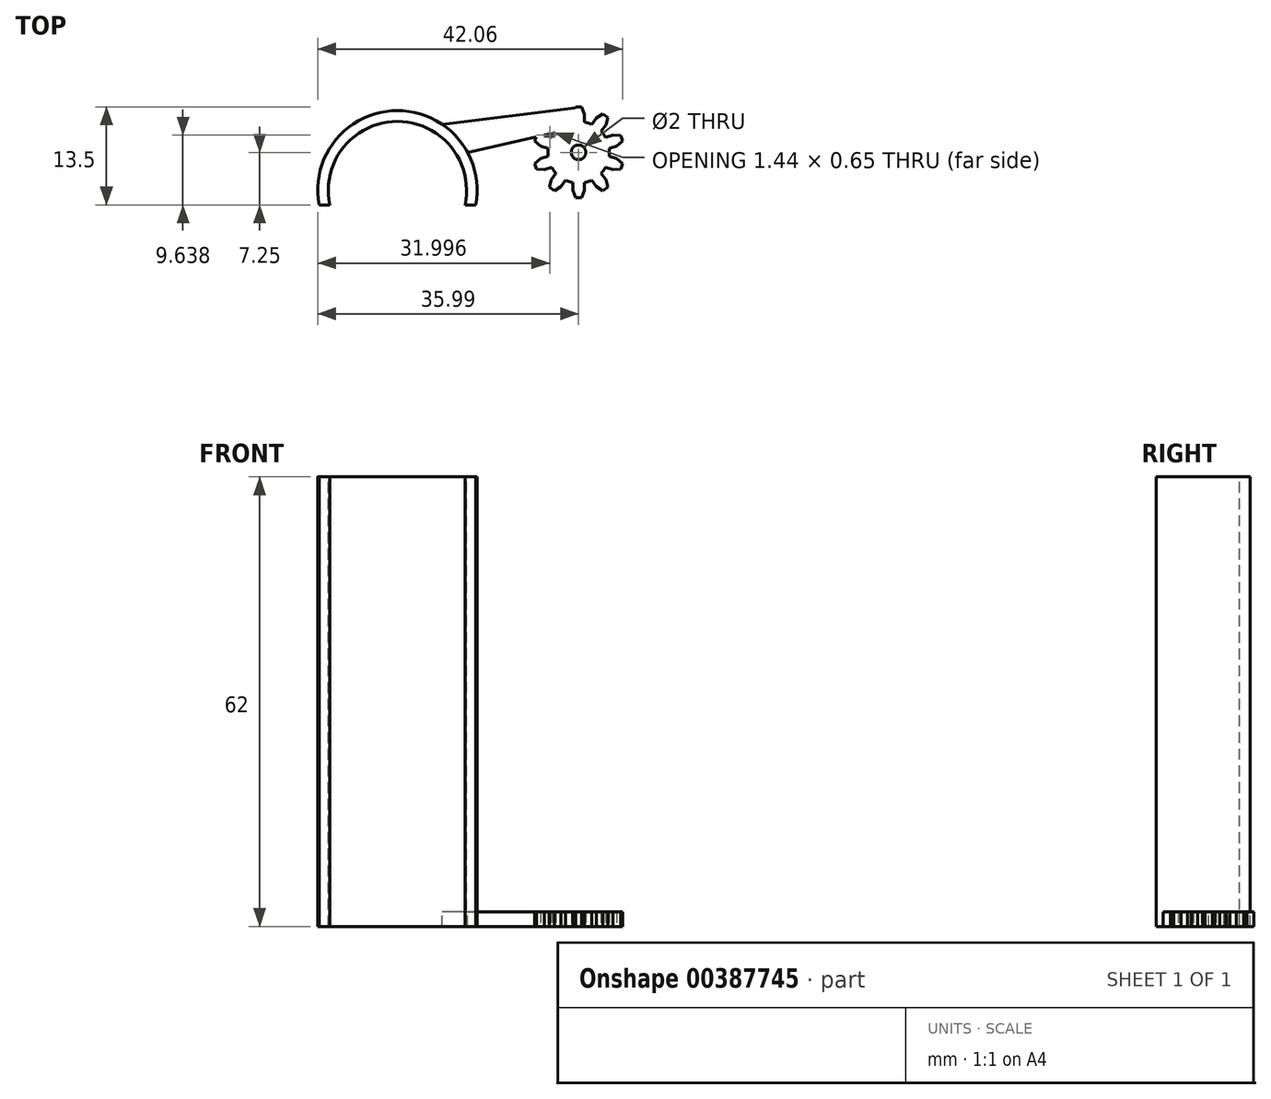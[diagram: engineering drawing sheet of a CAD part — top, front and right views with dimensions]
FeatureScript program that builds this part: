
annotation { "Feature Type Name" : "Feature", "Feature Type Description" : "" }
export const myFeature = defineFeature(function(context is Context, id is Id, definition is map)
    precondition{}
    {
        {
            var Q0;
            Q0=qCreatedBy(makeId("Top.planeOp"),FACE);
            var sketch = newSketch(context, id + "F0", { "sketchPlane" : qUnion([Q0])});
            skArc(sketch, "E0", {"start": v(-3.1, 2.9) * mm, "mid": v(-3.44, 2.5) * mm, "end": v(-3.72, 2.06) * mm});
            skLineSegment(sketch, "E1", {"start": v(-1.31, 4.04) * mm, "end": v(0, 0) * mm, "construction": true});
            skLineSegment(sketch, "E2", {"start": v(1.31, 4.04) * mm, "end": v(0, 0) * mm, "construction": true});
            skLineSegment(sketch, "E3", {"start": v(0, 0) * mm, "end": v(0, 4.25) * mm, "construction": true});
            skLineSegment(sketch, "E4", {"start": v(0, 4.25) * mm, "end": v(1.31, 4.04) * mm, "construction": true});
            skLineSegment(sketch, "E5", {"start": v(0, 4.25) * mm, "end": v(-1.31, 4.04) * mm, "construction": true});
            skLineSegment(sketch, "E6", {"start": v(-0.81, 5.26) * mm, "end": v(-0.4, 6.25) * mm});
            skLineSegment(sketch, "E7", {"start": v(0.4, 6.25) * mm, "end": v(0.81, 5.26) * mm});
            skLineSegment(sketch, "E8", {"start": v(0, 4.25) * mm, "end": v(0, 7.25) * mm, "construction": true});
            skLineSegment(sketch, "E9", {"start": v(-0.4, 6.25) * mm, "end": v(0.4, 6.25) * mm});
            skLineSegment(sketch, "E10", {"start": v(-1.31, 4.04) * mm, "end": v(1.31, 4.04) * mm, "construction": true});
            skLineSegment(sketch, "E11", {"start": v(0.81, 5.26) * mm, "end": v(0.81, 4.17) * mm});
            skLineSegment(sketch, "E12", {"start": v(-0.81, 5.26) * mm, "end": v(-0.81, 4.17) * mm});
            skLineSegment(sketch, "E13.1.0", {"start": v(-4, 4.82) * mm, "end": v(-3.34, 5.3) * mm});
            skLineSegment(sketch, "E13.1.1", {"start": v(-3.75, 3.78) * mm, "end": v(-4, 4.82) * mm});
            skLineSegment(sketch, "E13.1.2", {"start": v(-3.75, 3.78) * mm, "end": v(-3.1, 2.9) * mm});
            skLineSegment(sketch, "E13.1.3", {"start": v(-3.34, 5.3) * mm, "end": v(-2.44, 4.74) * mm});
            skLineSegment(sketch, "E13.1.4", {"start": v(-2.44, 4.74) * mm, "end": v(-1.8, 3.85) * mm});
            skLineSegment(sketch, "E13.2.0", {"start": v(-6.07, 1.54) * mm, "end": v(-5.82, 2.32) * mm});
            skLineSegment(sketch, "E13.2.1", {"start": v(-5.26, 0.85) * mm, "end": v(-6.07, 1.54) * mm});
            skLineSegment(sketch, "E13.2.2", {"start": v(-5.26, 0.85) * mm, "end": v(-4.22, 0.52) * mm});
            skLineSegment(sketch, "E13.2.3", {"start": v(-5.82, 2.32) * mm, "end": v(-4.75, 2.4) * mm});
            skLineSegment(sketch, "E13.2.4", {"start": v(-4.75, 2.4) * mm, "end": v(-3.72, 2.06) * mm});
            skLineSegment(sketch, "E13.3.0", {"start": v(-5.82, -2.32) * mm, "end": v(-6.07, -1.54) * mm});
            skLineSegment(sketch, "E13.3.1", {"start": v(-4.75, -2.4) * mm, "end": v(-5.82, -2.32) * mm});
            skLineSegment(sketch, "E13.3.2", {"start": v(-4.75, -2.4) * mm, "end": v(-3.72, -2.06) * mm});
            skLineSegment(sketch, "E13.3.3", {"start": v(-6.07, -1.54) * mm, "end": v(-5.26, -0.85) * mm});
            skLineSegment(sketch, "E13.3.4", {"start": v(-5.26, -0.85) * mm, "end": v(-4.22, -0.52) * mm});
            skLineSegment(sketch, "E13.4.0", {"start": v(-3.34, -5.3) * mm, "end": v(-4, -4.82) * mm});
            skLineSegment(sketch, "E13.4.1", {"start": v(-2.44, -4.74) * mm, "end": v(-3.34, -5.3) * mm});
            skLineSegment(sketch, "E13.4.2", {"start": v(-2.44, -4.74) * mm, "end": v(-1.8, -3.85) * mm});
            skLineSegment(sketch, "E13.4.3", {"start": v(-4, -4.82) * mm, "end": v(-3.75, -3.78) * mm});
            skLineSegment(sketch, "E13.4.4", {"start": v(-3.75, -3.78) * mm, "end": v(-3.1, -2.9) * mm});
            skLineSegment(sketch, "E13.5.0", {"start": v(0.4, -6.25) * mm, "end": v(-0.4, -6.25) * mm});
            skLineSegment(sketch, "E13.5.1", {"start": v(0.81, -5.26) * mm, "end": v(0.4, -6.25) * mm});
            skLineSegment(sketch, "E13.5.2", {"start": v(0.81, -5.26) * mm, "end": v(0.81, -4.17) * mm});
            skLineSegment(sketch, "E13.5.3", {"start": v(-0.4, -6.25) * mm, "end": v(-0.81, -5.26) * mm});
            skLineSegment(sketch, "E13.5.4", {"start": v(-0.81, -5.26) * mm, "end": v(-0.81, -4.17) * mm});
            skLineSegment(sketch, "E13.6.0", {"start": v(4, -4.82) * mm, "end": v(3.34, -5.3) * mm});
            skLineSegment(sketch, "E13.6.1", {"start": v(3.75, -3.78) * mm, "end": v(4, -4.82) * mm});
            skLineSegment(sketch, "E13.6.2", {"start": v(3.75, -3.78) * mm, "end": v(3.1, -2.9) * mm});
            skLineSegment(sketch, "E13.6.3", {"start": v(3.34, -5.3) * mm, "end": v(2.44, -4.74) * mm});
            skLineSegment(sketch, "E13.6.4", {"start": v(2.44, -4.74) * mm, "end": v(1.8, -3.85) * mm});
            skLineSegment(sketch, "E13.7.0", {"start": v(6.07, -1.54) * mm, "end": v(5.82, -2.32) * mm});
            skLineSegment(sketch, "E13.7.1", {"start": v(5.26, -0.85) * mm, "end": v(6.07, -1.54) * mm});
            skLineSegment(sketch, "E13.7.2", {"start": v(5.26, -0.85) * mm, "end": v(4.22, -0.52) * mm});
            skLineSegment(sketch, "E13.7.3", {"start": v(5.82, -2.32) * mm, "end": v(4.75, -2.4) * mm});
            skLineSegment(sketch, "E13.7.4", {"start": v(4.75, -2.4) * mm, "end": v(3.72, -2.06) * mm});
            skLineSegment(sketch, "E13.8.0", {"start": v(5.82, 2.32) * mm, "end": v(6.07, 1.54) * mm});
            skLineSegment(sketch, "E13.8.1", {"start": v(4.75, 2.4) * mm, "end": v(5.82, 2.32) * mm});
            skLineSegment(sketch, "E13.8.2", {"start": v(4.75, 2.4) * mm, "end": v(3.72, 2.06) * mm});
            skLineSegment(sketch, "E13.8.3", {"start": v(6.07, 1.54) * mm, "end": v(5.26, 0.85) * mm});
            skLineSegment(sketch, "E13.8.4", {"start": v(5.26, 0.85) * mm, "end": v(4.22, 0.52) * mm});
            skLineSegment(sketch, "E13.9.0", {"start": v(3.34, 5.3) * mm, "end": v(4, 4.82) * mm});
            skLineSegment(sketch, "E13.9.1", {"start": v(2.44, 4.74) * mm, "end": v(3.34, 5.3) * mm});
            skLineSegment(sketch, "E13.9.2", {"start": v(2.44, 4.74) * mm, "end": v(1.8, 3.85) * mm});
            skLineSegment(sketch, "E13.9.3", {"start": v(4, 4.82) * mm, "end": v(3.75, 3.78) * mm});
            skLineSegment(sketch, "E13.9.4", {"start": v(3.75, 3.78) * mm, "end": v(3.1, 2.9) * mm});
            skCircle(sketch, "E14", {"center": v(0, 0) * mm, "radius": 1 * mm});
            skArc(sketch, "E15.trimOffspring", {"start": v(-4.22, 0.52) * mm, "mid": v(-4.25, 0) * mm, "end": v(-4.22, -0.52) * mm});
            skArc(sketch, "E16.trimOffspring", {"start": v(-3.72, -2.06) * mm, "mid": v(-3.44, -2.5) * mm, "end": v(-3.1, -2.9) * mm});
            skArc(sketch, "E17.trimOffspring", {"start": v(-1.8, -3.85) * mm, "mid": v(-1.31, -4.04) * mm, "end": v(-0.81, -4.17) * mm});
            skArc(sketch, "E18.trimOffspring", {"start": v(0.81, -4.17) * mm, "mid": v(1.31, -4.04) * mm, "end": v(1.8, -3.85) * mm});
            skArc(sketch, "E19.trimOffspring", {"start": v(3.1, -2.9) * mm, "mid": v(3.44, -2.5) * mm, "end": v(3.72, -2.06) * mm});
            skArc(sketch, "E20.trimOffspring", {"start": v(4.22, -0.52) * mm, "mid": v(4.25, 0) * mm, "end": v(4.22, 0.52) * mm});
            skArc(sketch, "E21.trimOffspring", {"start": v(3.72, 2.06) * mm, "mid": v(3.44, 2.5) * mm, "end": v(3.1, 2.9) * mm});
            skArc(sketch, "E22.trimOffspring", {"start": v(1.8, 3.85) * mm, "mid": v(1.31, 4.04) * mm, "end": v(0.81, 4.17) * mm});
            skArc(sketch, "E23.trimOffspring", {"start": v(-0.81, 4.17) * mm, "mid": v(-1.31, 4.04) * mm, "end": v(-1.8, 3.85) * mm});
            skSolve(sketch);
        }
        {
            var Q0;
            Q0=makeQuery(id+"F0.imprint","IMPRINT",FACE,{"disambiguationData":[TD([[makeQuery(id+"F0.imprint","IMPRINT",EDGE,{"derivedFrom":sQuery(id+"F0.wireOp",EDGE,"E0")}),1.0]])]});
            extrude(context, id + "F1", {"entities" : qUnion([Q0]), "depth" : 2 * mm});
        }
        {
            var Q0;
            Q0=makeQuery(id+"F1.opExtrude","CAP_FACE",FACE,{"disambiguationData":[OSD([sQuery(id+"F0.wireOp",EDGE,"E0"),sQuery(id+"F0.wireOp",EDGE,"E6"),sQuery(id+"F0.wireOp",EDGE,"E7"),sQuery(id+"F0.wireOp",EDGE,"E9"),sQuery(id+"F0.wireOp",EDGE,"E11"),sQuery(id+"F0.wireOp",EDGE,"E12"),sQuery(id+"F0.wireOp",EDGE,"E13.1.0"),sQuery(id+"F0.wireOp",EDGE,"E13.1.1"),sQuery(id+"F0.wireOp",EDGE,"E13.1.2"),sQuery(id+"F0.wireOp",EDGE,"E13.1.3"),sQuery(id+"F0.wireOp",EDGE,"E13.1.4"),sQuery(id+"F0.wireOp",EDGE,"E13.2.0"),sQuery(id+"F0.wireOp",EDGE,"E13.2.1"),sQuery(id+"F0.wireOp",EDGE,"E13.2.2"),sQuery(id+"F0.wireOp",EDGE,"E13.2.3"),sQuery(id+"F0.wireOp",EDGE,"E13.2.4"),sQuery(id+"F0.wireOp",EDGE,"E13.3.0"),sQuery(id+"F0.wireOp",EDGE,"E13.3.1"),sQuery(id+"F0.wireOp",EDGE,"E13.3.2"),sQuery(id+"F0.wireOp",EDGE,"E13.3.3"),sQuery(id+"F0.wireOp",EDGE,"E13.3.4"),sQuery(id+"F0.wireOp",EDGE,"E13.4.0"),sQuery(id+"F0.wireOp",EDGE,"E13.4.1"),sQuery(id+"F0.wireOp",EDGE,"E13.4.2"),sQuery(id+"F0.wireOp",EDGE,"E13.4.3"),sQuery(id+"F0.wireOp",EDGE,"E13.4.4"),sQuery(id+"F0.wireOp",EDGE,"E13.5.0"),sQuery(id+"F0.wireOp",EDGE,"E13.5.1"),sQuery(id+"F0.wireOp",EDGE,"E13.5.2"),sQuery(id+"F0.wireOp",EDGE,"E13.5.3"),sQuery(id+"F0.wireOp",EDGE,"E13.5.4"),sQuery(id+"F0.wireOp",EDGE,"E13.6.0"),sQuery(id+"F0.wireOp",EDGE,"E13.6.1"),sQuery(id+"F0.wireOp",EDGE,"E13.6.2"),sQuery(id+"F0.wireOp",EDGE,"E13.6.3"),sQuery(id+"F0.wireOp",EDGE,"E13.6.4"),sQuery(id+"F0.wireOp",EDGE,"E13.7.0"),sQuery(id+"F0.wireOp",EDGE,"E13.7.1"),sQuery(id+"F0.wireOp",EDGE,"E13.7.2"),sQuery(id+"F0.wireOp",EDGE,"E13.7.3"),sQuery(id+"F0.wireOp",EDGE,"E13.7.4"),sQuery(id+"F0.wireOp",EDGE,"E13.8.0"),sQuery(id+"F0.wireOp",EDGE,"E13.8.1"),sQuery(id+"F0.wireOp",EDGE,"E13.8.2"),sQuery(id+"F0.wireOp",EDGE,"E13.8.3"),sQuery(id+"F0.wireOp",EDGE,"E13.8.4"),sQuery(id+"F0.wireOp",EDGE,"E13.9.0"),sQuery(id+"F0.wireOp",EDGE,"E13.9.1"),sQuery(id+"F0.wireOp",EDGE,"E13.9.2"),sQuery(id+"F0.wireOp",EDGE,"E13.9.3"),sQuery(id+"F0.wireOp",EDGE,"E13.9.4"),sQuery(id+"F0.wireOp",EDGE,"E14"),sQuery(id+"F0.wireOp",EDGE,"E15.trimOffspring"),sQuery(id+"F0.wireOp",EDGE,"E16.trimOffspring"),sQuery(id+"F0.wireOp",EDGE,"E17.trimOffspring"),sQuery(id+"F0.wireOp",EDGE,"E18.trimOffspring"),sQuery(id+"F0.wireOp",EDGE,"E19.trimOffspring"),sQuery(id+"F0.wireOp",EDGE,"E20.trimOffspring"),sQuery(id+"F0.wireOp",EDGE,"E21.trimOffspring"),sQuery(id+"F0.wireOp",EDGE,"E22.trimOffspring"),sQuery(id+"F0.wireOp",EDGE,"E23.trimOffspring")])],"isStart":false});
            var sketch = newSketch(context, id + "F2", { "sketchPlane" : qUnion([Q0])});
            skArc(sketch, "E24", {"start": v(-15.68, -7.25) * mm, "mid": v(-24.99, 4.27) * mm, "end": v(-34.3, -7.25) * mm});
            skArc(sketch, "E25", {"start": v(-14.17, -7.25) * mm, "mid": v(-14.12, -3.53) * mm, "end": v(-15.32, 0) * mm});
            skLineSegment(sketch, "E26", {"start": v(-35.8, -7.25) * mm, "end": v(-34.3, -7.25) * mm});
            skLineSegment(sketch, "E27", {"start": v(-15.68, -7.25) * mm, "end": v(-14.17, -7.25) * mm});
            skLineSegment(sketch, "E28", {"start": v(-15.32, 0) * mm, "end": v(1.8, 3.85) * mm});
            skLineSegment(sketch, "E29", {"start": v(1.8, 3.85) * mm, "end": v(0.4, 6.25) * mm});
            skLineSegment(sketch, "E30", {"start": v(0.4, 6.25) * mm, "end": v(-18.81, 3.85) * mm});
            skArc(sketch, "E31.trimOffspring", {"start": v(-18.81, 3.85) * mm, "mid": v(-31, 3.96) * mm, "end": v(-35.8, -7.25) * mm});
            skSolve(sketch);
        }
        {
            var Q0;
            Q0=makeQuery(id+"F2.imprint","IMPRINT",FACE,{"disambiguationData":[TD([[makeQuery(id+"F2.imprint","IMPRINT",EDGE,{"derivedFrom":sQuery(id+"F2.wireOp",EDGE,"E24")}),-1.0]])]});
            extrude(context, id + "F3", {"entities" : qUnion([Q0]), "operationType" : NewBodyOperationType.ADD, "oppositeDirection" : true, "depth" : 2 * mm});
        }
        {
            var Q0;
            {var subQ0=sQuery(id+"F0.wireOp",EDGE,"E23.trimOffspring");var subQ1=sQuery(id+"F0.wireOp",EDGE,"E13.2.4");var subQ2=sQuery(id+"F0.wireOp",EDGE,"E13.2.3");var subQ3=sQuery(id+"F0.wireOp",EDGE,"E13.2.0");var subQ4=sQuery(id+"F0.wireOp",EDGE,"E13.1.4");var subQ5=sQuery(id+"F0.wireOp",EDGE,"E13.1.3");var subQ6=sQuery(id+"F0.wireOp",EDGE,"E13.1.2");var subQ7=sQuery(id+"F0.wireOp",EDGE,"E13.1.1");var subQ8=sQuery(id+"F0.wireOp",EDGE,"E13.1.0");var subQ9=sQuery(id+"F0.wireOp",EDGE,"E12");var subQ10=sQuery(id+"F0.wireOp",EDGE,"E6");var subQ11=sQuery(id+"F0.wireOp",EDGE,"E0");Q0=makeQuery(id+"F3.boolean.opBoolean","MERGE",FACE,{"derivedFrom":[makeQuery(id+"F1.opExtrude","CAP_FACE",FACE,{"disambiguationData":[OSD([subQ11,subQ10,sQuery(id+"F0.wireOp",EDGE,"E7"),sQuery(id+"F0.wireOp",EDGE,"E9"),sQuery(id+"F0.wireOp",EDGE,"E11"),subQ9,subQ8,subQ7,subQ6,subQ5,subQ4,subQ3,sQuery(id+"F0.wireOp",EDGE,"E13.2.1"),sQuery(id+"F0.wireOp",EDGE,"E13.2.2"),subQ2,subQ1,sQuery(id+"F0.wireOp",EDGE,"E13.3.0"),sQuery(id+"F0.wireOp",EDGE,"E13.3.1"),sQuery(id+"F0.wireOp",EDGE,"E13.3.2"),sQuery(id+"F0.wireOp",EDGE,"E13.3.3"),sQuery(id+"F0.wireOp",EDGE,"E13.3.4"),sQuery(id+"F0.wireOp",EDGE,"E13.4.0"),sQuery(id+"F0.wireOp",EDGE,"E13.4.1"),sQuery(id+"F0.wireOp",EDGE,"E13.4.2"),sQuery(id+"F0.wireOp",EDGE,"E13.4.3"),sQuery(id+"F0.wireOp",EDGE,"E13.4.4"),sQuery(id+"F0.wireOp",EDGE,"E13.5.0"),sQuery(id+"F0.wireOp",EDGE,"E13.5.1"),sQuery(id+"F0.wireOp",EDGE,"E13.5.2"),sQuery(id+"F0.wireOp",EDGE,"E13.5.3"),sQuery(id+"F0.wireOp",EDGE,"E13.5.4"),sQuery(id+"F0.wireOp",EDGE,"E13.6.0"),sQuery(id+"F0.wireOp",EDGE,"E13.6.1"),sQuery(id+"F0.wireOp",EDGE,"E13.6.2"),sQuery(id+"F0.wireOp",EDGE,"E13.6.3"),sQuery(id+"F0.wireOp",EDGE,"E13.6.4"),sQuery(id+"F0.wireOp",EDGE,"E13.7.0"),sQuery(id+"F0.wireOp",EDGE,"E13.7.1"),sQuery(id+"F0.wireOp",EDGE,"E13.7.2"),sQuery(id+"F0.wireOp",EDGE,"E13.7.3"),sQuery(id+"F0.wireOp",EDGE,"E13.7.4"),sQuery(id+"F0.wireOp",EDGE,"E13.8.0"),sQuery(id+"F0.wireOp",EDGE,"E13.8.1"),sQuery(id+"F0.wireOp",EDGE,"E13.8.2"),sQuery(id+"F0.wireOp",EDGE,"E13.8.3"),sQuery(id+"F0.wireOp",EDGE,"E13.8.4"),sQuery(id+"F0.wireOp",EDGE,"E13.9.0"),sQuery(id+"F0.wireOp",EDGE,"E13.9.1"),sQuery(id+"F0.wireOp",EDGE,"E13.9.2"),sQuery(id+"F0.wireOp",EDGE,"E13.9.3"),sQuery(id+"F0.wireOp",EDGE,"E13.9.4"),sQuery(id+"F0.wireOp",EDGE,"E14"),sQuery(id+"F0.wireOp",EDGE,"E15.trimOffspring"),sQuery(id+"F0.wireOp",EDGE,"E16.trimOffspring"),sQuery(id+"F0.wireOp",EDGE,"E17.trimOffspring"),sQuery(id+"F0.wireOp",EDGE,"E18.trimOffspring"),sQuery(id+"F0.wireOp",EDGE,"E19.trimOffspring"),sQuery(id+"F0.wireOp",EDGE,"E20.trimOffspring"),sQuery(id+"F0.wireOp",EDGE,"E21.trimOffspring"),sQuery(id+"F0.wireOp",EDGE,"E22.trimOffspring"),subQ0])],"isStart":false}),makeQuery(id+"F3.opExtrude","CAP_FACE",FACE,{"disambiguationData":[OSD([subQ11,subQ10,subQ9,subQ8,subQ7,subQ6,subQ5,subQ4,subQ3,subQ2,subQ1,subQ0,sQuery(id+"F2.wireOp",EDGE,"E24"),sQuery(id+"F2.wireOp",EDGE,"E25"),sQuery(id+"F2.wireOp",EDGE,"E26"),sQuery(id+"F2.wireOp",EDGE,"E27"),sQuery(id+"F2.wireOp",EDGE,"E28"),sQuery(id+"F2.wireOp",EDGE,"E30"),sQuery(id+"F2.wireOp",EDGE,"E31.trimOffspring")])],"isStart":true})]});}
            var sketch = newSketch(context, id + "F4", { "sketchPlane" : qUnion([Q0])});
            skArc(sketch, "E32", {"start": v(-14.17, -7.25) * mm, "mid": v(-24.99, 5.75) * mm, "end": v(-35.8, -7.25) * mm});
            skPoint(sketch, "E32.first.point", {"position": v(-35.23, -1.23) * mm});
            skPoint(sketch, "E32.second.point", {"position": v(-32.93, 2.36) * mm});
            skPoint(sketch, "E32.third.point", {"position": v(-26.2, 5.68) * mm});
            skArc(sketch, "E33", {"start": v(-15.68, -7.25) * mm, "mid": v(-24.99, 4.28) * mm, "end": v(-34.3, -7.25) * mm});
            skPoint(sketch, "E33.first.point", {"position": v(-33.87, -1.81) * mm});
            skPoint(sketch, "E33.second.point", {"position": v(-27.8, 3.85) * mm});
            skPoint(sketch, "E33.third.point", {"position": v(-18.81, 2) * mm});
            skLineSegment(sketch, "E34", {"start": v(-35.8, -7.25) * mm, "end": v(-34.3, -7.25) * mm});
            skLineSegment(sketch, "E35", {"start": v(-15.68, -7.25) * mm, "end": v(-14.17, -7.25) * mm});
            skSolve(sketch);
        }
        {
            var Q0;
            Q0=makeQuery(id+"F4.imprint","IMPRINT",FACE,{"disambiguationData":[TD([[makeQuery(id+"F4.imprint","IMPRINT",EDGE,{"derivedFrom":sQuery(id+"F4.wireOp",EDGE,"E33")}),-1.0]])]});
            extrude(context, id + "F5", {"entities" : qUnion([Q0]), "operationType" : NewBodyOperationType.ADD, "depth" : 60 * mm});
        }
    });
